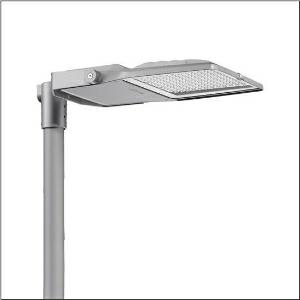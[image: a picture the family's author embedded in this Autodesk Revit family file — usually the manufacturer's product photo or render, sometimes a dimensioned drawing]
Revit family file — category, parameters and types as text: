
# Revit family: floodlight_fl_21_midi___pl52_5xa7785e2d3a_ba97
name_source: partatom
category: Lighting Fixtures
units: mm (PartAtom-declared; Revit-internal decimal feet)

## family parameters
Cut with Voids When Loaded = No
Host = Face
Light Source = No
Part Type = Normal
Room Calculation Point = No
Round Connector Dimension = Use Diameter
Shared = No

## types (1)
- --- (1 x LED, 26940 lm, 212.4 W, 3000K)
    Apparent Load = 212 VA
    CIE Flux Codes = 26 60 98 100 100
    Color Rendering = 70
    Color Temperature = 3000K
    Default Elevation = 1800 mm
    Description = Floodlight FL 21 midi, floodlight, primary light control with lens, of PMMA, primary optical cover: protective disc, of toughened safety glass, transparent, light distribution: PL52, light emission: direct distribution, installation type: surface-mounted, LED, High Power LED, rated luminous flux: 26.940lm, luminous efficacy: 127lm/W, light colour: 730, colour temperature: 3000K, control gear: Smart Interface (Zhaga), control: flexible luminous flux parameterisation, time-dependent luminous flux control, constant luminous flux control, overheat protection, pre-setting: logarithmic dimming characteristic, with terminal, 6-pole, mains connection: 220..240V, AC, 50/60Hz, start of lifetime: 212W, end of service life: 231W, reduction: 95W, luminaire housing, of diecast aluminium, powder-coated, Siteco® metallic grey (DB 702S), corrosivity category C5 mid according to DIN EN ISO 12944, suitable for swimming pools, chlorine-resistant, sealing non-destructively replaceable, please order mast flange separately, mast bracket, of steel, galvanised, powder-coated, Siteco® metallic grey (DB 702S), Smart Interface above, protection rating (complete): IP66, insulation class (complete): insulation class II (safety insulation), certification: CE, ENEC, VDE, protection symbol: D, impact resistance: IK08, permissible operating ambient temperature: -20..+40°C, permissible operating ambient temperature for outdoor applications: -40..+50°C, standard: DIN EN 12944, LABS conformity tested according to VDMA 24364:2018-05, packaging unit: 1 piece

Light Distribution: PL52
    Height = 76 mm
    Lamp = 1 x LED
    Lamp Light Flux = 26940 lm
    Lamp Power = 212.4 W
    Lamp count = 1
    Length = 657 mm
    Luminous efficacy = 127 lm/W
    Manufacturer = Siteco
    ModVariant = No
    Model = 5XA7785E2D3A
    Number of Poles = 1
    OnlyDefault = Yes
    Power Factor = 1
    Product Name = Floodlight FL 21 midi | PL52
    Product group = floodlight | pylon annexe
    ProductGroupID = 6201
    Protection Class = Protection class II
    Protection Degree = IP 66
    RLX_Detail_Level = 1
    RLX_Emergency_Light_Flux = 0 lm
    RLX_Emergency_Type = 0
    RLX_Emergency_Type_DB = No
    RlxData = <blob elided: 153717 chars, md5=811b39fb>
    Socket = socket
    Standby Power = 0 W
    System Light Flux = 26940 lm
    System Power = 212 W
    Type Comments = factory setting: luminous flux: 100 % | dim-lin: 254 | 710 mA
    Type Image = l_1007123.jpg
    URL = http://relux.com
    VarID = @adj_199099
    Voltage = 0 V
    Weight = 0.00 kg
    Width = 442 mm

## geometry (parser evidence)
native form markers: Blend x4, Sweep x15
no freeform markers — native parametric forms only
